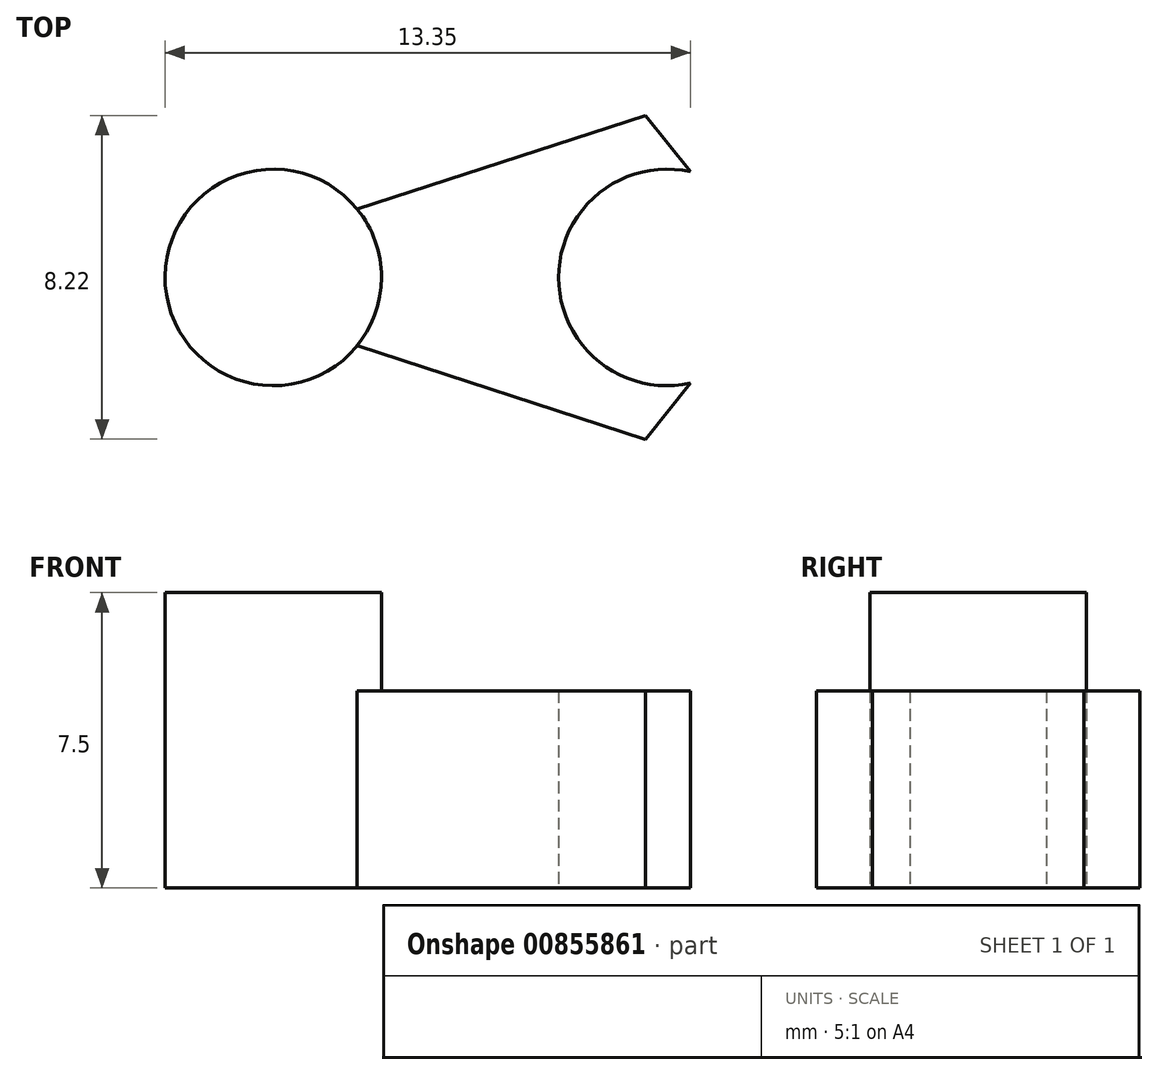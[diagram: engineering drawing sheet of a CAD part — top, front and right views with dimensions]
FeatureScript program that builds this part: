
annotation { "Feature Type Name" : "Feature", "Feature Type Description" : "" }
export const myFeature = defineFeature(function(context is Context, id is Id, definition is map)
    precondition{}
    {
        {
            var Q0;
            Q0=qCreatedBy(makeId("Top.planeOp"),FACE);
            var sketch = newSketch(context, id + "F0", { "sketchPlane" : qUnion([Q0])});
            skLineSegment(sketch, "E0", {"start": v(2.71, 4.11) * mm, "end": v(3.85, 2.68) * mm});
            skLineSegment(sketch, "E1", {"start": v(3.85, -2.68) * mm, "end": v(2.71, -4.11) * mm});
            skArc(sketch, "E2", {"start": v(3.85, 2.68) * mm, "mid": v(0.5, 0) * mm, "end": v(3.85, -2.68) * mm});
            skArc(sketch, "E3", {"start": v(-4.61, 1.73) * mm, "mid": v(-9.5, 0) * mm, "end": v(-4.61, -1.73) * mm});
            skPoint(sketch, "E4.orphan", {"position": v(-6, 0) * mm});
            skPoint(sketch, "E5.orphan", {"position": v(6, 0) * mm});
            skLineSegment(sketch, "E6", {"start": v(3.85, 2.54) * mm, "end": v(3.85, -2.27) * mm, "construction": true});
            skLineSegment(sketch, "E7", {"start": v(3.85, 2.68) * mm, "end": v(3.85, 2.68) * mm});
            skLineSegment(sketch, "E8", {"start": v(3.85, -2.68) * mm, "end": v(3.85, -2.68) * mm});
            skLineSegment(sketch, "E9", {"start": v(-4.61, -1.73) * mm, "end": v(2.71, -4.11) * mm});
            skLineSegment(sketch, "E10", {"start": v(-4.61, 1.73) * mm, "end": v(2.71, 4.11) * mm});
            skPoint(sketch, "E11.MirrorCS.start.orphan", {"position": v(0, 7.5) * mm});
            skPoint(sketch, "E12.MirrorCS.end.orphan", {"position": v(0, -7.5) * mm});
            skSolve(sketch);
        }
        {
            var Q0;
            Q0 = qSketchRegion(id + "F0", true);
            extrude(context, id + "F1", {"entities" : qUnion([Q0]), "endBound" : BoundingType.SYMMETRIC, "depth" : 5 * mm, "offsetDistance" : 25 * mm});
        }
        {
            var Q0;
            Q0=makeQuery(id+"F1.opExtrude","CAP_FACE",FACE,{"disambiguationData":[OSD([sQuery(id+"F0.wireOp",EDGE,"E0"),sQuery(id+"F0.wireOp",EDGE,"E1"),sQuery(id+"F0.wireOp",EDGE,"E12.MirrorCS"),sQuery(id+"F0.wireOp",EDGE,"E11.MirrorCS"),sQuery(id+"F0.wireOp",EDGE,"E2"),sQuery(id+"F0.wireOp",EDGE,"E3"),sQuery(id+"F0.wireOp",EDGE,"E7"),sQuery(id+"F0.wireOp",EDGE,"E8")])],"isStart":false});
            var sketch = newSketch(context, id + "F2", { "sketchPlane" : qUnion([Q0])});
            skLineSegment(sketch, "E13.0", {"start": v(-4.61, 1.73) * mm, "end": v(-4.61, 1.73) * mm});
            skCircle(sketch, "E14", {"center": v(-6.75, 0) * mm, "radius": 2.75 * mm});
            skSolve(sketch);
        }
        {
            var Q0;
            Q0 = qSketchRegion(id + "F2", true);
            extrude(context, id + "F3", {"entities" : qUnion([Q0]), "operationType" : NewBodyOperationType.ADD, "depth" : 2.5 * mm, "offsetDistance" : 25 * mm});
        }
    });
